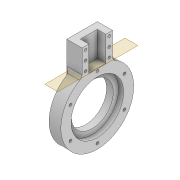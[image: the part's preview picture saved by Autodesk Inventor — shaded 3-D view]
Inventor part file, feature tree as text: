
AUTODESK INVENTOR PART (.ipt)
format: ipt  version: 2022 (Build 260153000, 153)  size: 214,016 bytes
history: native  units: mm
features: extrude x7, sketch x6, fillet x2, pattern_circular x1, plane x1, mirror x1, projected_geometry x1
ambient origin geometry x8: Origin, YZ Plane, XZ Plane, XY Plane, X Axis, Y Axis, Z Axis, Center Point
bodies: Solid1 (feature_tree)
feature tree (19):
  extrude  "Extrusion1"  Depth=12.0mm
  extrude  "Extrusion2"  Depth=8.0mm TaperAngle=0.0deg
  extrude  "Extrusion3"  Depth=6.0mm TaperAngle=0.0deg
  pattern_circular  "Circular Pattern1"  Count=10  [1 undecoded]
  plane  "Work Plane1"
  sketch  "Sketch4"  dims[d8=3.2mm]
  extrude  "Extrusion4"  Depth=5.0mm
  extrude  "Extrusion5"  Depth=10.1mm
  fillet  "Fillet1"  Radius=20.2mm
  extrude  "Extrusion6"  Depth=10.1mm
  fillet  "Fillet2"  Radius=8.0mm
  extrude  "Extrusion7"  Depth=8.0mm
  mirror  "Mirror1"
  sketch  "Sketch1"  dims[d0=62.5mm d1=12.0mm]
  sketch  "Sketch2"  dims[d2=50.0mm d3=8.0mm d4=0.0mm]
  projected_geometry  "Projected Loop1"
  sketch  "Sketch3"  dims[d5=62.5mm d6=6.0mm d7=0.0mm]
  sketch  "Sketch6"  dims[d9=37.0mm d10=100.0mm d11=0.0mm]
  sketch  "Sketch7"  dims[d12=60.0mm d13=360.0deg d15=40.0mm d16=10.1mm d17=20.2mm d18=10.1mm d20=8.0mm d21=8.0mm d22=100.0mm d23=0.0mm d24=30.0mm d25=0.0mm d26=5.0mm d27=3.2mm d28=3.2mm d29=3.2mm d30=4.0mm d31=4.0mm d32=15.0mm d33=4.0mm d34=9.0mm d35=4.0mm d36=0.0mm d37=5.0mm d38=100.0mm d39=0.0mm]
note: 1 required parameter value undecoded (feature->parameter linkage not recoverable at this tier; creation-order binding heuristic only, values carry confidence <= 0.55)
